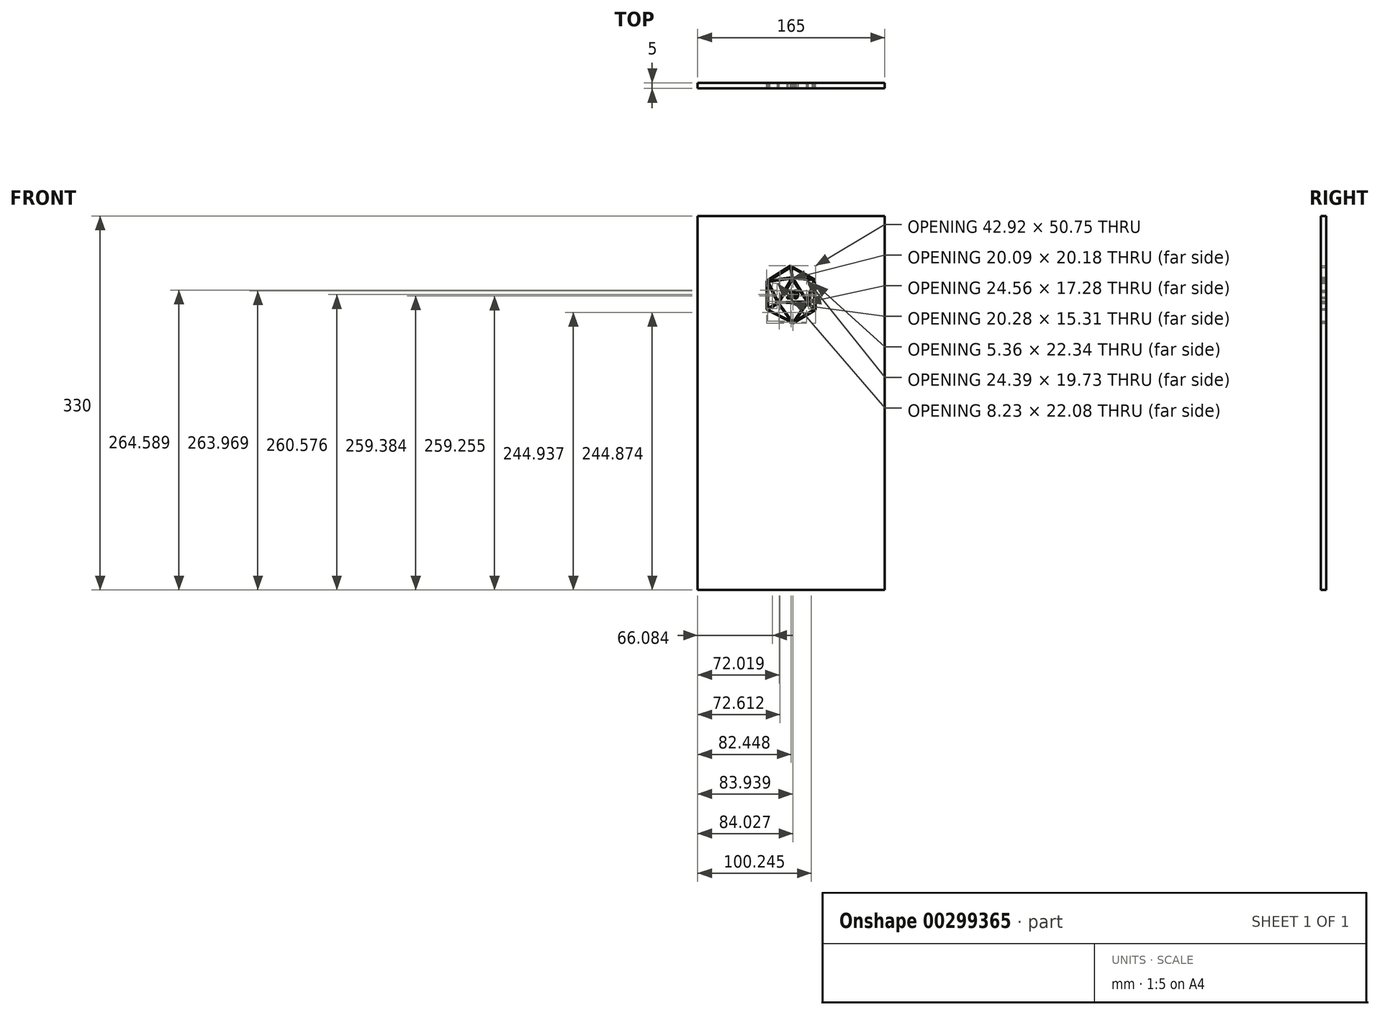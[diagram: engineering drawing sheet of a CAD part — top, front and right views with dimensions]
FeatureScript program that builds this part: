
annotation { "Feature Type Name" : "Feature", "Feature Type Description" : "" }
export const myFeature = defineFeature(function(context is Context, id is Id, definition is map)
    precondition{}
    {
        {
            var Q0;
            Q0=qCreatedBy(makeId("Front.planeOp"),FACE);
            var sketch = newSketch(context, id + "F0", { "sketchPlane" : qUnion([Q0])});
            skLineSegment(sketch, "E0.bottom", {"start": v(-75.2, 235.78) * mm, "end": v(89.8, 235.78) * mm});
            skLineSegment(sketch, "E0.top", {"start": v(-75.2, -94.22) * mm, "end": v(89.8, -94.22) * mm});
            skLineSegment(sketch, "E0.left", {"start": v(-75.2, 235.78) * mm, "end": v(-75.2, -94.22) * mm});
            skLineSegment(sketch, "E0.right", {"start": v(89.8, 235.78) * mm, "end": v(89.8, -94.22) * mm});
            skLineSegment(sketch, "E1", {"start": v(8.9, 140.98) * mm, "end": v(28.7, 152.74) * mm});
            skLineSegment(sketch, "E2", {"start": v(10.64, 143.06) * mm, "end": v(27.14, 152.97) * mm});
            skLineSegment(sketch, "E3", {"start": v(21.74, 158.9) * mm, "end": v(27.14, 152.97) * mm});
            skLineSegment(sketch, "E4", {"start": v(10.64, 143.06) * mm, "end": v(21.74, 158.9) * mm});
            skLineSegment(sketch, "E5", {"start": v(8.9, 142.01) * mm, "end": v(21.02, 159.3) * mm});
            skLineSegment(sketch, "E6", {"start": v(21.02, 159.3) * mm, "end": v(-3.54, 158.9) * mm});
            skLineSegment(sketch, "E7", {"start": v(-3.54, 158.9) * mm, "end": v(8.9, 142.01) * mm});
            skLineSegment(sketch, "E8", {"start": v(6.96, 143.06) * mm, "end": v(-4.32, 158.37) * mm});
            skLineSegment(sketch, "E9", {"start": v(-4.32, 158.37) * mm, "end": v(-13.32, 152.97) * mm});
            skLineSegment(sketch, "E10", {"start": v(-13.32, 152.97) * mm, "end": v(6.96, 143.06) * mm});
            skLineSegment(sketch, "E11", {"start": v(8.9, 140.98) * mm, "end": v(-14.21, 152.97) * mm});
            skLineSegment(sketch, "E12", {"start": v(22.37, 159.78) * mm, "end": v(27.72, 153.87) * mm});
            skLineSegment(sketch, "E13", {"start": v(22.37, 159.78) * mm, "end": v(27.37, 176.2) * mm});
            skLineSegment(sketch, "E14", {"start": v(27.37, 176.2) * mm, "end": v(27.72, 153.87) * mm});
            skLineSegment(sketch, "E15", {"start": v(27.2, 179) * mm, "end": v(21.63, 160.72) * mm});
            skLineSegment(sketch, "E16", {"start": v(9.23, 180.47) * mm, "end": v(21.63, 160.72) * mm});
            skLineSegment(sketch, "E17", {"start": v(9.23, 180.47) * mm, "end": v(27.2, 179) * mm});
            skLineSegment(sketch, "E18", {"start": v(-3.37, 159.88) * mm, "end": v(21.02, 160.28) * mm});
            skLineSegment(sketch, "E19", {"start": v(-3.37, 159.88) * mm, "end": v(8.29, 179.61) * mm});
            skLineSegment(sketch, "E20", {"start": v(8.29, 179.61) * mm, "end": v(21.02, 160.28) * mm});
            skLineSegment(sketch, "E21", {"start": v(-4.22, 160.28) * mm, "end": v(-12.63, 177.62) * mm});
            skLineSegment(sketch, "E22", {"start": v(-12.63, 177.62) * mm, "end": v(7.5, 180.47) * mm});
            skLineSegment(sketch, "E23", {"start": v(7.5, 180.52) * mm, "end": v(-4.22, 160.28) * mm});
            skLineSegment(sketch, "E24", {"start": v(-13.23, 154.13) * mm, "end": v(-5, 159.3) * mm});
            skLineSegment(sketch, "E25", {"start": v(-5, 159.3) * mm, "end": v(-13.2, 176.2) * mm});
            skLineSegment(sketch, "E26", {"start": v(-13.2, 176.2) * mm, "end": v(-13.23, 154.13) * mm});
            skLineSegment(sketch, "E27", {"start": v(-11.49, 179) * mm, "end": v(7.85, 181.54) * mm});
            skLineSegment(sketch, "E28", {"start": v(7.85, 181.54) * mm, "end": v(6.7, 190.34) * mm});
            skLineSegment(sketch, "E29", {"start": v(6.65, 190.33) * mm, "end": v(-11.49, 179) * mm});
            skLineSegment(sketch, "E30", {"start": v(7.6, 190.21) * mm, "end": v(8.9, 181.44) * mm});
            skLineSegment(sketch, "E31", {"start": v(8.9, 181.44) * mm, "end": v(26.15, 180.04) * mm});
            skLineSegment(sketch, "E32", {"start": v(26.14, 179.97) * mm, "end": v(7.6, 190.21) * mm});
            skLineSegment(sketch, "E33", {"start": v(6.7, 191.73) * mm, "end": v(28.22, 179.84) * mm});
            skLineSegment(sketch, "E34", {"start": v(28.2, 179.8) * mm, "end": v(28.7, 152.74) * mm});
            skLineSegment(sketch, "E35", {"start": v(-14.21, 152.97) * mm, "end": v(-14.21, 178.4) * mm});
            skLineSegment(sketch, "E36", {"start": v(-14.21, 178.4) * mm, "end": v(6.7, 191.73) * mm});
            skLineSegment(sketch, "E37", {"start": v(6.7, 190.34) * mm, "end": v(-11.49, 179) * mm});
            skText(sketch, "E38", { "text": "20", "fontName": "Tinos-Bold.ttf"});
            skLineSegment(sketch, "E39", {"start": v(28.22, 179.84) * mm, "end": v(6.7, 191.73) * mm});
            skLineSegment(sketch, "E40", {"start": v(28.22, 179.84) * mm, "end": v(28.7, 152.74) * mm});
            skLineSegment(sketch, "E41", {"start": v(-14.21, 178.4) * mm, "end": v(-14.21, 152.97) * mm});
            const initialGuessF0  = {"E38": [0.0033, 0.16306, 1, 0, 0.00758]};
            skSetInitialGuess(sketch, initialGuessF0);
            skSolve(sketch);
        }
        {
            var Q0;
            Q0=makeQuery(id+"F0.imprint","IMPRINT",FACE,{"disambiguationData":[TD([[makeQuery(id+"F0.imprint","IMPRINT",EDGE,{"derivedFrom":sQuery(id+"F0.wireOp",EDGE,"E2")}),-1.0]])]});
            var Q1;
            Q1=makeQuery(id+"F0.imprint","IMPRINT",FACE,{"disambiguationData":[TD([[makeQuery(id+"F0.imprint","IMPRINT",EDGE,{"derivedFrom":sQuery(id+"F0.wireOp",EDGE,"E38.sketch_text.stroke-23")}),-1.0]])]});
            var Q2;
            Q2=makeQuery(id+"F0.imprint","IMPRINT",FACE,{"disambiguationData":[TD([[makeQuery(id+"F0.imprint","IMPRINT",EDGE,{"derivedFrom":sQuery(id+"F0.wireOp",EDGE,"E38.sketch_text.stroke-0")}),-1.0]])]});
            extrude(context, id + "F1", {"entities" : qUnion([Q0, Q1, Q2]), "depth" : 4.5 * mm, "offsetDistance" : 25 * mm});
        }
        {
            var Q0;
            Q0=makeQuery(id+"F0.imprint","IMPRINT",FACE,{"disambiguationData":[TD([[makeQuery(id+"F0.imprint","IMPRINT",EDGE,{"derivedFrom":sQuery(id+"F0.wireOp",EDGE,"E0.bottom")}),-1.0]])]});
            var Q1;
            Q1=makeQuery(id+"F0.imprint","IMPRINT",FACE,{"disambiguationData":[TD([[makeQuery(id+"F0.imprint","IMPRINT",EDGE,{"derivedFrom":sQuery(id+"F0.wireOp",EDGE,"E8")}),1.0]])]});
            var Q2;
            Q2=makeQuery(id+"F0.imprint","IMPRINT",FACE,{"disambiguationData":[TD([[makeQuery(id+"F0.imprint","IMPRINT",EDGE,{"derivedFrom":sQuery(id+"F0.wireOp",EDGE,"E24")}),1.0]])]});
            var Q3;
            {var subQ0=sQuery(id+"F0.wireOp",EDGE,"E21");Q3=makeQuery(id+"F0.imprint","IMPRINT",FACE,{"disambiguationData":[TD([[makeQuery(id+"F0.imprint","IMPRINT",EDGE,{"derivedFrom":subQ0}),-1.0]])]});}
            var Q4;
            Q4=makeQuery(id+"F0.imprint","IMPRINT",FACE,{"disambiguationData":[TD([[makeQuery(id+"F0.imprint","IMPRINT",EDGE,{"derivedFrom":sQuery(id+"F0.wireOp",EDGE,"E27")}),1.0]])]});
            var Q5;
            {var subQ0=sQuery(id+"F0.wireOp",EDGE,"E30");Q5=makeQuery(id+"F0.imprint","IMPRINT",FACE,{"disambiguationData":[TD([[makeQuery(id+"F0.imprint","IMPRINT",EDGE,{"derivedFrom":subQ0}),1.0]])]});}
            var Q6;
            Q6=makeQuery(id+"F0.imprint","IMPRINT",FACE,{"disambiguationData":[TD([[makeQuery(id+"F0.imprint","IMPRINT",EDGE,{"derivedFrom":sQuery(id+"F0.wireOp",EDGE,"E15")}),-1.0]])]});
            var Q7;
            Q7=makeQuery(id+"F0.imprint","IMPRINT",FACE,{"disambiguationData":[TD([[makeQuery(id+"F0.imprint","IMPRINT",EDGE,{"derivedFrom":sQuery(id+"F0.wireOp",EDGE,"E12")}),1.0]])]});
            var Q8;
            Q8=makeQuery(id+"F0.imprint","IMPRINT",FACE,{"disambiguationData":[TD([[makeQuery(id+"F0.imprint","IMPRINT",EDGE,{"derivedFrom":sQuery(id+"F0.wireOp",EDGE,"E2")}),1.0]])]});
            var Q9;
            Q9=makeQuery(id+"F0.imprint","IMPRINT",FACE,{"disambiguationData":[TD([[makeQuery(id+"F0.imprint","IMPRINT",EDGE,{"derivedFrom":sQuery(id+"F0.wireOp",EDGE,"E5")}),1.0]])]});
            var Q10;
            Q10=makeQuery(id+"F0.imprint","IMPRINT",FACE,{"disambiguationData":[TD([[makeQuery(id+"F0.imprint","IMPRINT",EDGE,{"derivedFrom":sQuery(id+"F0.wireOp",EDGE,"E18")}),1.0]])]});
            extrude(context, id + "F2", {"entities" : qUnion([Q0, Q1, Q2, Q3, Q4, Q5, Q6, Q7, Q8, Q9, Q10]), "depth" : 5 * mm, "offsetDistance" : 25 * mm});
        }
    });
